# Revit family: Furniture_Office-Chairs_Flokk_Giroflex-161
name_source: partatom
category: Furniture
units: mm (PartAtom-declared; Revit-internal decimal feet)

## family parameters
Always vertical = Yes
Cut with Voids When Loaded = No
OmniClass Number = 23.40.20.14.14.11
OmniClass Title = Chairs
Room Calculation Point = No
Shared = No
Work Plane-Based = No

## types (1)
- Giroflex 161
    AssetType = Movable
    BIMObjectName = Furniture_Office-Chairs_Flokk_Giroflex-161
    Brand = Flokk
    Category = Giroflex
    Color = Various
    Cost = 0 $
    Default Elevation = 0 mm  [stored 0 ft]
    Description = The giroflex161 is Ideal for any uses and suitable for a variety of interiors. The users sit comfortably and as a visitors chair the 161 will match perfectly with all Giroflex swivel chairs.

Special Collection Knit161 The 161 comes in a wide variety of options and colours. This version is a Special collection called Knit161. An exclusive selection of five perfectly matching colour-combinations. All Inspired by Swiss nature – authentic, and in harmony with the environment which we love to care for.
    Designer = Big Game
    DurationUnit = Year
    Features = The back mesh Knit161 is developed in polyester and especially for the giroflex 161. The slightly transparent design of the mesh gives the back a unique lightness, and your back is supported comfortably in the right places when you lean back.

The Selected seat cover is deivered in comfortable wool fabric from Gabriel. The densely woven relief structure gives the fabric visual depth and highlights the varied colours in a fine interplay of light and shade.
    IfcExportAs = IfcFurnishingElementType
    IfcExportType = CHAIR
    LowestSeatingHeight = 500 mm  [stored 1.64042 ft]
    MainColor = Various
    Manufacturer = Flokk
    ManufacturerName = Flokk
    ManufacturerURL = https://www.flokk.com
    Material = Plastic, Metal and Textile
    Model = Giroflex 161
    ModelNumber = 161-6403-KNI
    NBSDescription = Stacking chairs
    NBSReference = 45-35-20/355
    Name = Giroflex-161
    NominalDepth = 570 mm
    NominalLength = 575 mm
    OfficeChairQuaternaryMaterial = Basic Dark
    ProductDatasheet = https://flokkplatformprod.blob.core.windows.net
    ProductInformation = The visitor’s chair giroflex 161 is a cantilever-designed model that combines versatility with elegance and fits into any environment.
    SeatingHeight = 500 mm  [stored 1.64042 ft]
    Shape = Sculptured
    Size = 575x570x850 mm
    URL = https://store.flokk.com
    Uniclass2 = Pr_40_50_12_51
    Uniclass2015Description = Meeting room chairs
    Uniclass2015Reference = Pr_40_50_12_51
    Version = 1
    VersionDate = 20/12/2022
    WarrantyDurationUnit = Year

note: [stored X ft] marks values corroborated as IEEE doubles in the binary element streams (Revit-internal decimal feet)

## geometry (parser evidence)
native form markers: Sweep x5
no freeform markers — native parametric forms only
